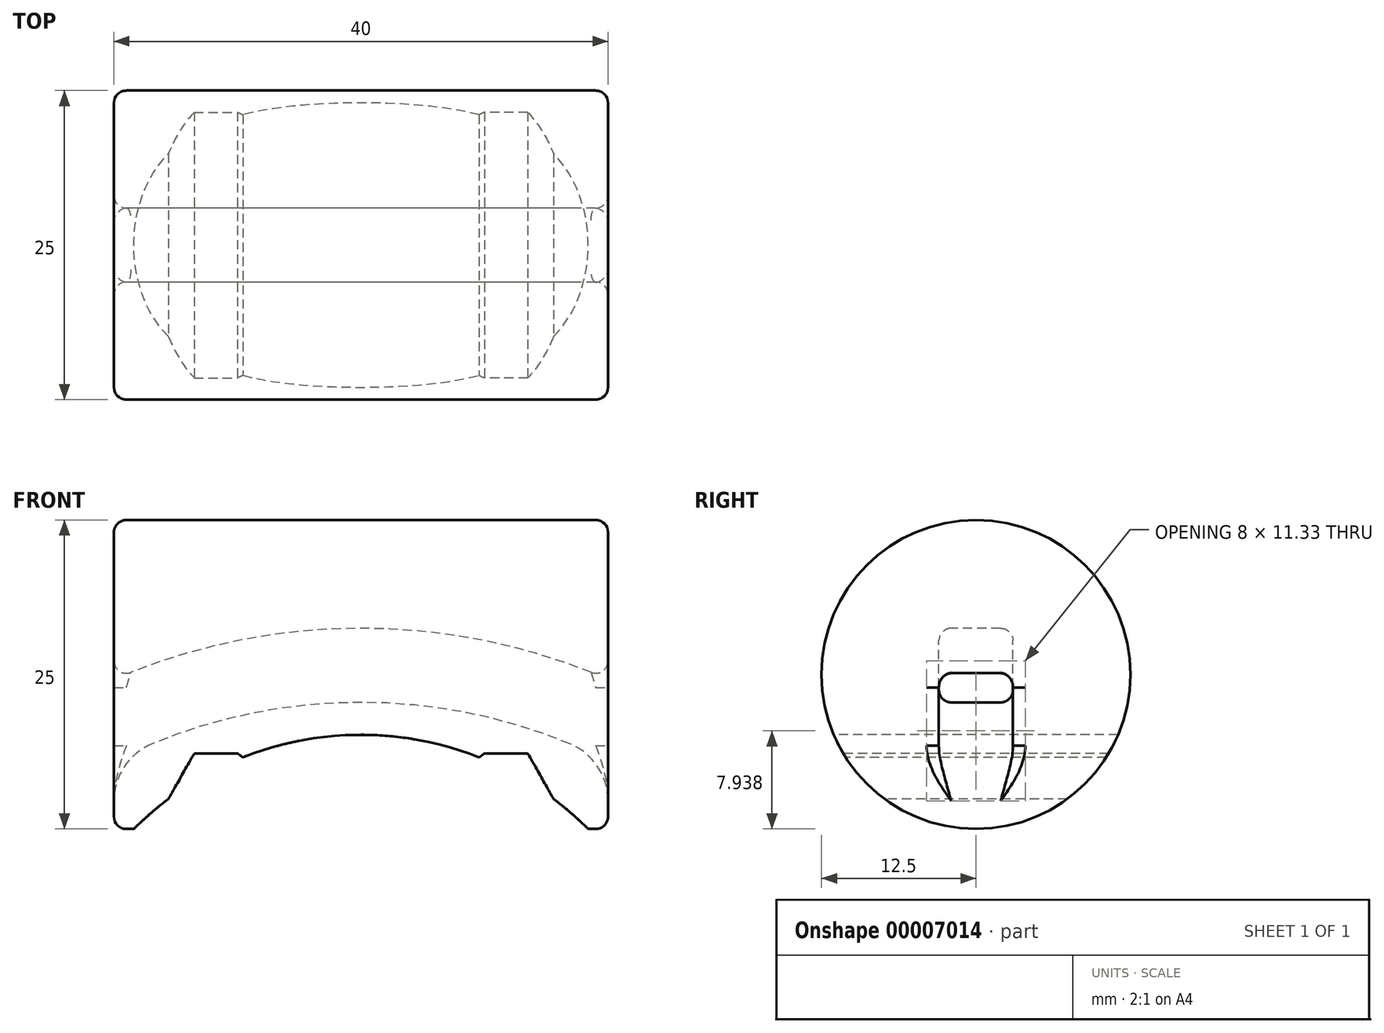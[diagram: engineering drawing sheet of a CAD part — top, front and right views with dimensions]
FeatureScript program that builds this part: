
annotation { "Feature Type Name" : "Feature", "Feature Type Description" : "" }
export const myFeature = defineFeature(function(context is Context, id is Id, definition is map)
    precondition{}
    {
        {
            var Q0;
            Q0=qCreatedBy(makeId("Right.planeOp"),FACE);
            var sketch = newSketch(context, id + "F0", { "sketchPlane" : qUnion([Q0])});
            skCircle(sketch, "E0", {"center": v(0, 0) * mm, "radius": 12.5 * mm});
            skSolve(sketch);
        }
        {
            var Q0;
            Q0 = qSketchRegion(id + "F0", true);
            var Q1;
            Q1=makeQuery(id+"F0.imprint","IMPRINT",FACE,{"disambiguationData":[TD([[makeQuery(id+"F0.imprint","IMPRINT",EDGE,{"derivedFrom":sQuery(id+"F0.wireOp",EDGE,"420fac4a-4768-4239-b4b7-bf044d38c6a5")}),1.0]])]});
            extrude(context, id + "F1", {"entities" : qUnion([Q0, Q1]), "depth" : 20 * mm});
        }
        {
            var Q0;
            Q0=qCreatedBy(makeId("Front.planeOp"),FACE);
            var sketch = newSketch(context, id + "F2", { "sketchPlane" : qUnion([Q0])});
            skCircle(sketch, "E1", {"center": v(0, -30.88) * mm, "radius": 26 * mm});
            skLineSegment(sketch, "E2", {"start": v(0, 0) * mm, "end": v(0, -4.88) * mm});
            skLineSegment(sketch, "E3", {"start": v(10, -6.88) * mm, "end": v(10, -6.38) * mm});
            skLineSegment(sketch, "E4", {"start": v(10, -6.38) * mm, "end": v(13.5, -6.38) * mm});
            skLineSegment(sketch, "E5", {"start": v(13.5, -6.38) * mm, "end": v(13.5, -8.66) * mm});
            skCircle(sketch, "E6", {"center": v(0, -46.68) * mm, "radius": 44.42 * mm});
            skCircle(sketch, "E7", {"center": v(0, -46.68) * mm, "radius": 50.42 * mm});
            skLineSegment(sketch, "E8", {"start": v(13.5, -6.38) * mm, "end": v(15.6, -10.07) * mm});
            skLineSegment(sketch, "E9", {"start": v(10, -6.38) * mm, "end": v(9.56, -6.7) * mm});
            skSolve(sketch);
        }
        {
            var Q0;
            {var subQ0=sQuery(id+"F2.wireOp",EDGE,"E1");var subQ2=makeQuery(id+"F2.imprint","IMPRINT",VERTEX,{"derivedFrom":subQ0});Q0=makeQuery(id+"F2.imprint","IMPRINT",FACE,{"disambiguationData":[TD([[makeQuery(id+"F2.imprint","IMPRINT",EDGE,{"disambiguationData":[TD([[subQ2,1.0]])],"derivedFrom":subQ0}),1.0]])]});}
            var Q1;
            {var subQ1=sQuery(id+"F2.wireOp",EDGE,"E3");Q1=makeQuery(id+"F2.imprint","IMPRINT",FACE,{"disambiguationData":[TD([[makeQuery(id+"F2.imprint","IMPRINT",EDGE,{"derivedFrom":subQ1}),-1.0]])]});}
            var Q2;
            {var subQ0=sQuery(id+"F2.wireOp",EDGE,"E5");Q2=makeQuery(id+"F2.imprint","IMPRINT",FACE,{"disambiguationData":[TD([[makeQuery(id+"F2.imprint","IMPRINT",EDGE,{"derivedFrom":subQ0}),1.0]])]});}
            var Q3;
            {var subQ0=sQuery(id+"F2.wireOp",EDGE,"E3");Q3=makeQuery(id+"F2.imprint","IMPRINT",FACE,{"disambiguationData":[TD([[makeQuery(id+"F2.imprint","IMPRINT",EDGE,{"derivedFrom":subQ0}),1.0]])]});}
            extrude(context, id + "F3", {"entities" : qUnion([Q0, Q1, Q2, Q3]), "operationType" : NewBodyOperationType.REMOVE, "endBound" : BoundingType.SYMMETRIC, "oppositeDirection" : true, "depth" : 53.8 * mm});
        }
        {
            var Q0;
            Q0=makeQuery(id+"F2.imprint","IMPRINT",FACE,{"disambiguationData":[TD([[makeQuery(id+"F2.imprint","IMPRINT",EDGE,{"derivedFrom":sQuery(id+"F2.wireOp",EDGE,"E6")}),-1.0]])]});
            extrude(context, id + "F4", {"entities" : qUnion([Q0]), "operationType" : NewBodyOperationType.REMOVE, "endBound" : BoundingType.SYMMETRIC, "oppositeDirection" : true, "depth" : 6 * mm});
        }
        {
            var Q0;
            Q0=makeQuery(id+"F4.boolean.opBoolean","INTERSECT",EDGE,{"derivedFrom":[makeQuery(id+"F1.opExtrude","CAP_FACE",FACE,{"disambiguationData":[OSD([sQuery(id+"F0.wireOp",EDGE,"E0")])],"isStart":false}),makeQuery(id+"F4.opExtrude","SWEPT_FACE",FACE,{"disambiguationData":[OSD([sQuery(id+"F2.wireOp",EDGE,"E6")])]})]});
            fillet(context, id + "F5", {"entities" : qUnion([Q0]), "radius" : 5 * mm, "tangentPropagation" : true, "allowEdgeOverflow" : false});
        }
        {
            var Q0;
            Q0=makeQuery(id+"F1.opExtrude","SWEPT_BODY",BODY,{"disambiguationData":[OSD([sQuery(id+"F0.wireOp",EDGE,"E0"),sQuery(id+"F0.wireOp",EDGE,"4e32b73e-326c-4121-aa8e-c481b77c35b4.bottom"),sQuery(id+"F0.wireOp",EDGE,"4e32b73e-326c-4121-aa8e-c481b77c35b4.top"),sQuery(id+"F0.wireOp",EDGE,"4e32b73e-326c-4121-aa8e-c481b77c35b4.left"),sQuery(id+"F0.wireOp",EDGE,"4e32b73e-326c-4121-aa8e-c481b77c35b4.right")])]});
            var Q1;
            Q1=qCreatedBy(makeId("Right.planeOp"),FACE);
            mirror(context, id + "F6", {"operationType" : NewBodyOperationType.ADD, "entities" : qUnion([Q0]), "mirrorPlane" : qUnion([Q1])});
        }
        {
            var Q0;
            Q0=makeQuery(id+"F6.opPattern","COPY",EDGE,{"derivedFrom":makeQuery(id+"F1.opExtrude","CAP_EDGE",EDGE,{"disambiguationData":[OSD([sQuery(id+"F0.wireOp",EDGE,"E0")])],"isStart":false}),"instanceName":"1"});
            var Q1;
            Q1=makeQuery(id+"F1.opExtrude","CAP_EDGE",EDGE,{"disambiguationData":[OSD([sQuery(id+"F0.wireOp",EDGE,"E0")])],"isStart":false});
            var Q2;
            Q2=makeQuery(id+"F4.boolean.opBoolean","INTERSECT",EDGE,{"derivedFrom":[makeQuery(id+"F1.opExtrude","CAP_FACE",FACE,{"disambiguationData":[OSD([sQuery(id+"F0.wireOp",EDGE,"E0")])],"isStart":false}),makeQuery(id+"F4.opExtrude","CAP_FACE",FACE,{"disambiguationData":[OSD([sQuery(id+"F2.wireOp",EDGE,"E6"),sQuery(id+"F2.wireOp",EDGE,"E7")])],"isStart":true})]});
            var Q3;
            Q3=makeQuery(id+"F4.boolean.opBoolean","INTERSECT",EDGE,{"derivedFrom":[makeQuery(id+"F1.opExtrude","CAP_FACE",FACE,{"disambiguationData":[OSD([sQuery(id+"F0.wireOp",EDGE,"E0")])],"isStart":false}),makeQuery(id+"F4.opExtrude","CAP_FACE",FACE,{"disambiguationData":[OSD([sQuery(id+"F2.wireOp",EDGE,"E6"),sQuery(id+"F2.wireOp",EDGE,"E7")])],"isStart":false})]});
            var Q4;
            Q4=makeQuery(id+"F4.boolean.opBoolean","INTERSECT",EDGE,{"derivedFrom":[makeQuery(id+"F1.opExtrude","CAP_FACE",FACE,{"disambiguationData":[OSD([sQuery(id+"F0.wireOp",EDGE,"E0")])],"isStart":false}),makeQuery(id+"F4.opExtrude","SWEPT_FACE",FACE,{"disambiguationData":[OSD([sQuery(id+"F2.wireOp",EDGE,"E7")])]})]});
            var Q5;
            Q5=makeQuery(id+"F6.opPattern","COPY",EDGE,{"derivedFrom":makeQuery(id+"F4.boolean.opBoolean","INTERSECT",EDGE,{"derivedFrom":[makeQuery(id+"F1.opExtrude","CAP_FACE",FACE,{"disambiguationData":[OSD([sQuery(id+"F0.wireOp",EDGE,"E0")])],"isStart":false}),makeQuery(id+"F4.opExtrude","CAP_FACE",FACE,{"disambiguationData":[OSD([sQuery(id+"F2.wireOp",EDGE,"E6"),sQuery(id+"F2.wireOp",EDGE,"E7")])],"isStart":false})]}),"instanceName":"1"});
            var Q6;
            Q6=makeQuery(id+"F6.opPattern","COPY",EDGE,{"derivedFrom":makeQuery(id+"F4.boolean.opBoolean","INTERSECT",EDGE,{"derivedFrom":[makeQuery(id+"F1.opExtrude","CAP_FACE",FACE,{"disambiguationData":[OSD([sQuery(id+"F0.wireOp",EDGE,"E0")])],"isStart":false}),makeQuery(id+"F4.opExtrude","SWEPT_FACE",FACE,{"disambiguationData":[OSD([sQuery(id+"F2.wireOp",EDGE,"E7")])]})]}),"instanceName":"1"});
            var Q7;
            Q7=makeQuery(id+"F6.opPattern","COPY",EDGE,{"derivedFrom":makeQuery(id+"F4.boolean.opBoolean","INTERSECT",EDGE,{"derivedFrom":[makeQuery(id+"F1.opExtrude","CAP_FACE",FACE,{"disambiguationData":[OSD([sQuery(id+"F0.wireOp",EDGE,"E0")])],"isStart":false}),makeQuery(id+"F4.opExtrude","CAP_FACE",FACE,{"disambiguationData":[OSD([sQuery(id+"F2.wireOp",EDGE,"E6"),sQuery(id+"F2.wireOp",EDGE,"E7")])],"isStart":true})]}),"instanceName":"1"});
            var Q8;
            {var subQ0=makeQuery(id+"F4.boolean.opBoolean","COPY",EDGE,{"derivedFrom":makeQuery(id+"F4.opExtrude","CAP_EDGE",EDGE,{"disambiguationData":[OSD([sQuery(id+"F2.wireOp",EDGE,"E7")])],"isStart":true})});Q8=makeQuery(id+"F6.boolean.opBoolean","MERGE",EDGE,{"derivedFrom":[subQ0,makeQuery(id+"F6.opPattern","COPY",EDGE,{"derivedFrom":subQ0,"instanceName":"1"})]});}
            var Q9;
            {var subQ0=makeQuery(id+"F4.boolean.opBoolean","COPY",EDGE,{"derivedFrom":makeQuery(id+"F4.opExtrude","CAP_EDGE",EDGE,{"disambiguationData":[OSD([sQuery(id+"F2.wireOp",EDGE,"E7")])],"isStart":false})});Q9=makeQuery(id+"F6.boolean.opBoolean","MERGE",EDGE,{"derivedFrom":[subQ0,makeQuery(id+"F6.opPattern","COPY",EDGE,{"derivedFrom":subQ0,"instanceName":"1"})]});}
            var Q10;
            {var subQ0=makeQuery(id+"F4.boolean.opBoolean","COPY",EDGE,{"derivedFrom":makeQuery(id+"F4.opExtrude","CAP_EDGE",EDGE,{"disambiguationData":[OSD([sQuery(id+"F2.wireOp",EDGE,"E6")])],"isStart":false})});Q10=makeQuery(id+"F6.boolean.opBoolean","MERGE",EDGE,{"derivedFrom":[subQ0,makeQuery(id+"F6.opPattern","COPY",EDGE,{"derivedFrom":subQ0,"instanceName":"1"})]});}
            var Q11;
            {var subQ0=makeQuery(id+"F4.boolean.opBoolean","COPY",EDGE,{"derivedFrom":makeQuery(id+"F4.opExtrude","CAP_EDGE",EDGE,{"disambiguationData":[OSD([sQuery(id+"F2.wireOp",EDGE,"E6")])],"isStart":true})});Q11=makeQuery(id+"F6.boolean.opBoolean","MERGE",EDGE,{"derivedFrom":[subQ0,makeQuery(id+"F6.opPattern","COPY",EDGE,{"derivedFrom":subQ0,"instanceName":"1"})]});}
            fillet(context, id + "F7", {"entities" : qUnion([Q0, Q1, Q2, Q3, Q4, Q5, Q6, Q7, Q8, Q9, Q10, Q11]), "radius" : 1 * mm, "tangentPropagation" : true, "allowEdgeOverflow" : false});
        }
    });
